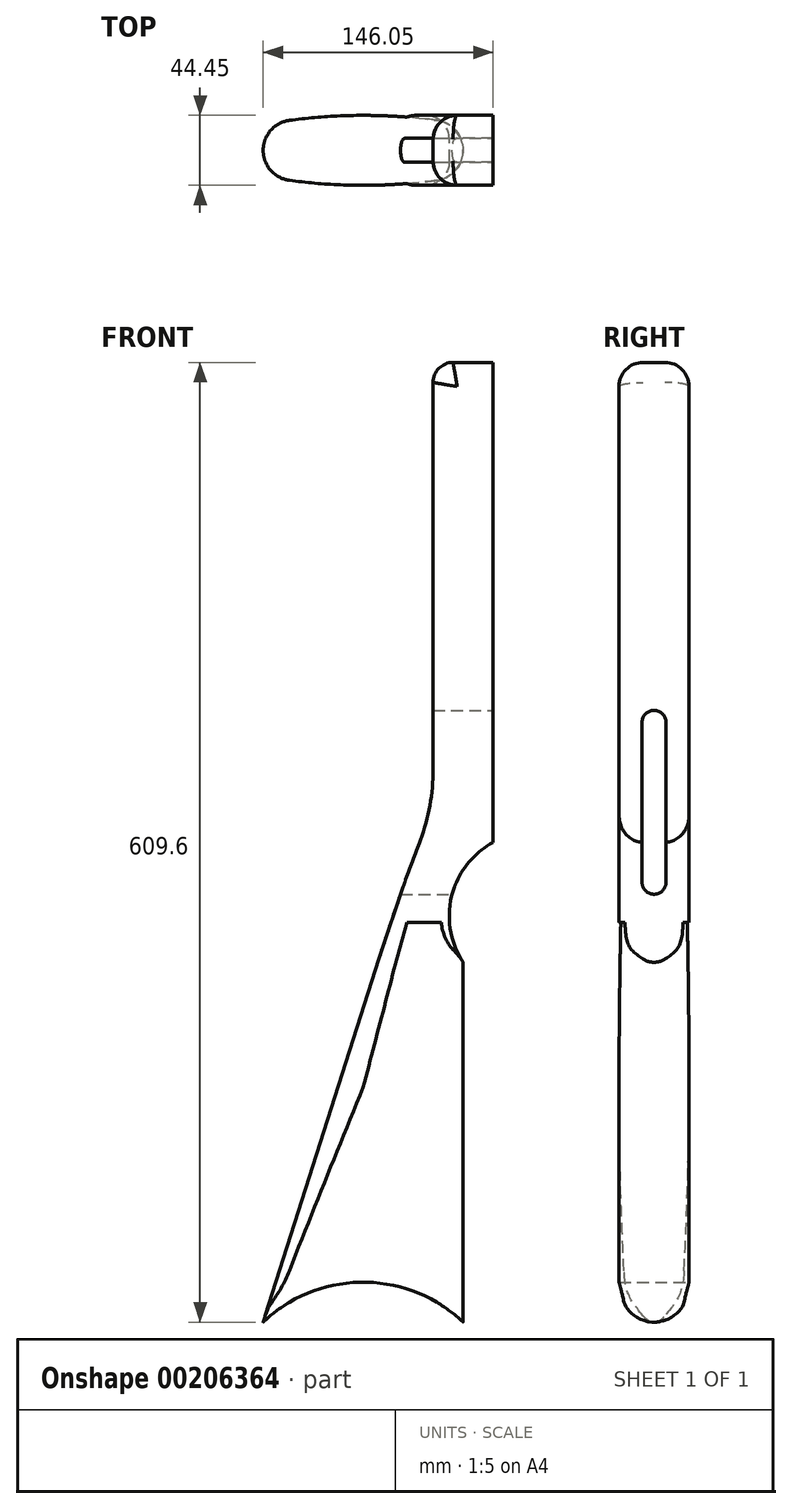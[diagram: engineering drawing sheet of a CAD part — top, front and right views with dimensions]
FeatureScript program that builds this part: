
annotation { "Feature Type Name" : "Feature", "Feature Type Description" : "" }
export const myFeature = defineFeature(function(context is Context, id is Id, definition is map)
    precondition{}
    {
        {
            var Q0;
            Q0=qCreatedBy(makeId("Front.planeOp"),FACE);
            var sketch = newSketch(context, id + "F0", { "sketchPlane" : qUnion([Q0])});
            skLineSegment(sketch, "E0.direction1", {"start": v(-1434.24, 1401.08) * mm, "end": v(-1408.84, 1401.08) * mm, "construction": true});
            skLineSegment(sketch, "E0.direction2", {"start": v(-1434.24, 1401.08) * mm, "end": v(-1434.24, 588.28) * mm, "construction": true});
            skLineSegment(sketch, "E1.1.0", {"start": v(69.19, 165.93) * mm, "end": v(69.19, -79.99) * mm});
            skArc(sketch, "E1.1.2", {"start": v(61, -124.82) * mm, "mid": v(47.45, -162.22) * mm, "end": v(34.87, -199.97) * mm});
            skLineSegment(sketch, "E1.1.3", {"start": v(34.87, -199.97) * mm, "end": v(-28, -397.22) * mm});
            skArc(sketch, "E1.1.4", {"start": v(107.29, -126.17) * mm, "mid": v(81.03, -160.1) * mm, "end": v(88.24, -202.37) * mm});
            skArc(sketch, "E1.1.5", {"start": v(69.19, -79.99) * mm, "mid": v(67.12, -102.77) * mm, "end": v(61, -124.82) * mm});
            skLineSegment(sketch, "E1.1.6", {"start": v(107.29, 178.63) * mm, "end": v(107.29, -126.17) * mm});
            skArc(sketch, "E1.1.9", {"start": v(88.24, -430.97) * mm, "mid": v(41.34, -407.08) * mm, "end": v(-10.98, -412.78) * mm});
            skLineSegment(sketch, "E1.1.11", {"start": v(88.24, -202.37) * mm, "end": v(88.24, -430.97) * mm});
            skLineSegment(sketch, "E1.1.14", {"start": v(24.74, -430.97) * mm, "end": v(24.74, -405.57) * mm, "construction": true});
            skArc(sketch, "E1.1.15", {"start": v(-28, -397.22) * mm, "mid": v(-24.47, -410.45) * mm, "end": v(-10.98, -412.78) * mm, "construction": true});
            skLineSegment(sketch, "E1.1.16", {"start": v(107.29, 178.63) * mm, "end": v(81.89, 178.63) * mm});
            skArc(sketch, "E1.1.17", {"start": v(-10.98, -412.78) * mm, "mid": v(-25.7, -420.61) * mm, "end": v(-38.76, -430.97) * mm});
            skArc(sketch, "E1.1.18", {"start": v(81.89, 178.63) * mm, "mid": v(72.9, 174.9) * mm, "end": v(69.19, 165.93) * mm});
            skLineSegment(sketch, "E2.direction1", {"start": v(107.29, -126.17) * mm, "end": v(116.81, -126.17) * mm, "construction": true});
            skLineSegment(sketch, "E3", {"start": v(-28, -397.22) * mm, "end": v(-38.76, -430.97) * mm});
            skSolve(sketch);
        }
        {
            var Q0;
            Q0 = qSketchRegion(id + "F0", true);
            extrude(context, id + "F1", {"entities" : qUnion([Q0]), "depth" : 44.45 * mm});
        }
        {
            var Q0;
            Q0=makeQuery(id+"F1.opExtrude","SWEPT_FACE",FACE,{"disambiguationData":[OSD([sQuery(id+"F0.wireOp",EDGE,"E1.1.16")])]});
            var sketch = newSketch(context, id + "F2", { "sketchPlane" : qUnion([Q0])});
            skLineSegment(sketch, "E4", {"start": v(66.65, 0) * mm, "end": v(66.65, -44.95) * mm});
            skPoint(sketch, "E4.startSnap0", {"position": v(94.59, 0) * mm});
            skLineSegment(sketch, "E5", {"start": v(66.65, 0) * mm, "end": v(91.41, 0) * mm});
            skArc(sketch, "E6", {"start": v(91.41, 0) * mm, "mid": v(75.7, -6.5) * mm, "end": v(69.19, -22.23) * mm});
            skLineSegment(sketch, "E7", {"start": v(91.41, -22.23) * mm, "end": v(69.19, -22.23) * mm, "construction": true});
            skArc(sketch, "E8.MirrorCS", {"start": v(91.41, -44.45) * mm, "mid": v(75.7, -37.94) * mm, "end": v(69.19, -22.23) * mm});
            skLineSegment(sketch, "E9.MirrorCS", {"start": v(66.65, -44.45) * mm, "end": v(91.41, -44.45) * mm});
            skSolve(sketch);
        }
        {
            var Q0;
            Q0=makeQuery(id+"F1.opExtrude","CAP_EDGE",EDGE,{"disambiguationData":[OSD([sQuery(id+"F0.wireOp",EDGE,"E1.1.2")])],"isStart":true});
            var Q1;
            Q1=makeQuery(id+"F1.opExtrude","CAP_EDGE",EDGE,{"disambiguationData":[OSD([sQuery(id+"F0.wireOp",EDGE,"E1.1.0")])],"isStart":false});
            var Q2;
            Q2=makeQuery(id+"F1.opExtrude","CAP_EDGE",EDGE,{"disambiguationData":[OSD([sQuery(id+"F0.wireOp",EDGE,"E1.1.4")])],"isStart":false});
            var Q3;
            Q3=makeQuery(id+"F1.opExtrude","CAP_EDGE",EDGE,{"disambiguationData":[OSD([sQuery(id+"F0.wireOp",EDGE,"E1.1.4")])],"isStart":true});
            fillet(context, id + "F3", {"entities" : qUnion([Q0, Q1, Q2, Q3]), "radius" : 15.24 * mm, "tangentPropagation" : true, "allowEdgeOverflow" : false});
        }
        {
            var Q0;
            Q0=makeQuery(id+"F1.opExtrude","CAP_VERTEX",VERTEX,{"disambiguationData":[OSD([sQuery(id+"F0.wireOp",EDGE,"E1.1.9"),sQuery(id+"F0.wireOp",EDGE,"E1.1.11")])],"isStart":false});
            var Q1;
            Q1=makeQuery(id+"F1.opExtrude","CAP_VERTEX",VERTEX,{"disambiguationData":[OSD([sQuery(id+"F0.wireOp",EDGE,"E1.1.9"),sQuery(id+"F0.wireOp",EDGE,"E1.1.11")])],"isStart":true});
            var Q2;
            {var subQ0=sQuery(id+"F0.wireOp",EDGE,"E3");var subQ1=sQuery(id+"F0.wireOp",EDGE,"E1.1.3");Q2=makeQuery(id+"F3.opFillet","BLEND_VERTEX",VERTEX,{"blendedFrom":[makeQuery(id+"F1.opExtrude","CAP_EDGE",EDGE,{"disambiguationData":[OSD([subQ1,subQ0])],"isStart":false}),makeQuery(id+"F1.opExtrude","SWEPT_FACE",FACE,{"disambiguationData":[OSD([subQ1,subQ0])]}),makeQuery(id+"F1.opExtrude","SWEPT_FACE",FACE,{"disambiguationData":[OSD([sQuery(id+"F0.wireOp",EDGE,"E1.1.9"),sQuery(id+"F0.wireOp",EDGE,"E1.1.17")])]})],"blendedInto":[makeQuery(id+"F1.opExtrude","SWEPT_FACE",FACE,{"disambiguationData":[OSD([subQ1,subQ0])]}),makeQuery(id+"F1.opExtrude","SWEPT_FACE",FACE,{"disambiguationData":[OSD([sQuery(id+"F0.wireOp",EDGE,"E1.1.9"),sQuery(id+"F0.wireOp",EDGE,"E1.1.17")])]})]});}
            cPlane(context, id + "F4", {"entities" : qUnion([Q0, Q1, Q2]), "cplaneType" : CPlaneType.THREE_POINT, "offset" : 25.4 * mm, "width" : 152.4 * mm, "height" : 152.4 * mm});
        }
        {
            var Q0;
            Q0=qCreatedBy(id+"F4.planeOp",FACE);
            var sketch = newSketch(context, id + "F5", { "sketchPlane" : qUnion([Q0])});
            skLineSegment(sketch, "E10", {"start": v(-38.76, 22.23) * mm, "end": v(88.24, 22.23) * mm, "construction": true});
            skArc(sketch, "E11", {"start": v(88.24, 22.22) * mm, "mid": v(83.5, 34.87) * mm, "end": v(71.6, 41.27) * mm});
            skArc(sketch, "E12", {"start": v(71.6, 41.27) * mm, "mid": v(48.22, 43.66) * mm, "end": v(24.74, 44.45) * mm});
            skLineSegment(sketch, "E13", {"start": v(24.74, 44.45) * mm, "end": v(24.74, 22.23) * mm, "construction": true});
            skLineSegment(sketch, "E14", {"start": v(88.24, 44.45) * mm, "end": v(24.74, 44.45) * mm, "construction": true});
            skLineSegment(sketch, "E15", {"start": v(88.24, 22.22) * mm, "end": v(88.24, 0) * mm, "construction": true});
            skArc(sketch, "E16.MirrorCS", {"start": v(-22.13, 41.27) * mm, "mid": v(1.25, 43.66) * mm, "end": v(24.74, 44.45) * mm});
            skArc(sketch, "E17.MirrorCS", {"start": v(-38.76, 22.22) * mm, "mid": v(-34.02, 34.87) * mm, "end": v(-22.13, 41.27) * mm});
            skArc(sketch, "E18.MirrorCS", {"start": v(88.24, 22.23) * mm, "mid": v(83.5, 9.58) * mm, "end": v(71.6, 3.18) * mm});
            skArc(sketch, "E19.MirrorCS", {"start": v(71.6, 3.18) * mm, "mid": v(48.22, 0.8) * mm, "end": v(24.74, 0) * mm});
            skArc(sketch, "E20.MirrorCS", {"start": v(-22.13, 3.18) * mm, "mid": v(1.25, 0.8) * mm, "end": v(24.74, 0) * mm});
            skArc(sketch, "E21.MirrorCS", {"start": v(-38.76, 22.23) * mm, "mid": v(-34.02, 9.58) * mm, "end": v(-22.13, 3.18) * mm});
            skLineSegment(sketch, "E22.bottom", {"start": v(100.94, -12.7) * mm, "end": v(-51.46, -12.7) * mm});
            skLineSegment(sketch, "E22.top", {"start": v(100.94, 57.15) * mm, "end": v(-51.46, 57.15) * mm});
            skLineSegment(sketch, "E22.left", {"start": v(100.94, -12.7) * mm, "end": v(100.94, 57.15) * mm});
            skLineSegment(sketch, "E22.right", {"start": v(-51.46, -12.7) * mm, "end": v(-51.46, 57.15) * mm});
            skPoint(sketch, "E22.middle", {"position": v(24.74, 22.23) * mm});
            skSolve(sketch);
        }
        {
            var Q0;
            Q0 = qSketchRegion(id + "F5", true);
            extrude(context, id + "F6", {"entities" : qUnion([Q0]), "operationType" : NewBodyOperationType.REMOVE, "oppositeDirection" : true, "depth" : 254 * mm});
        }
        {
            var Q0;
            Q0=makeQuery(id+"F1.opExtrude","SWEPT_FACE",FACE,{"disambiguationData":[OSD([sQuery(id+"F0.wireOp",EDGE,"E1.1.6")])]});
            var sketch = newSketch(context, id + "F7", { "sketchPlane" : qUnion([Q0])});
            skLineSegment(sketch, "E23", {"start": v(-22.23, 178.63) * mm, "end": v(-22.23, -431.6) * mm, "construction": true});
            skLineSegment(sketch, "E24.bottom", {"start": v(-14.6, -151.57) * mm, "end": v(-29.84, -151.57) * mm, "construction": true});
            skLineSegment(sketch, "E24.top", {"start": v(-22.22, -49.97) * mm, "end": v(-29.84, -49.97) * mm, "construction": true});
            skLineSegment(sketch, "E24.left", {"start": v(-14.6, -151.57) * mm, "end": v(-14.6, -49.97) * mm});
            skLineSegment(sketch, "E24.right", {"start": v(-29.84, -151.57) * mm, "end": v(-29.84, -49.97) * mm});
            skPoint(sketch, "E24.middle", {"position": v(-22.22, -100.77) * mm});
            skArc(sketch, "E25", {"start": v(-14.6, -49.97) * mm, "mid": v(-22.22, -42.35) * mm, "end": v(-29.84, -49.97) * mm});
            skArc(sketch, "E26", {"start": v(-29.84, -151.57) * mm, "mid": v(-22.22, -159.2) * mm, "end": v(-14.6, -151.57) * mm});
            skSolve(sketch);
        }
        {
            var Q0;
            Q0 = qSketchRegion(id + "F7", true);
            extrude(context, id + "F8", {"entities" : qUnion([Q0]), "operationType" : NewBodyOperationType.REMOVE, "endBound" : BoundingType.THROUGH_ALL, "oppositeDirection" : true, "depth" : 25.4 * mm});
        }
    });
